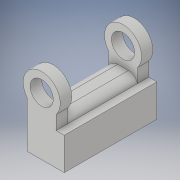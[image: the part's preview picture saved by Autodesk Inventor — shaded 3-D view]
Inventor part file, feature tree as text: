
AUTODESK INVENTOR PART (.ipt)
format: ipt  version: 2019 (Build 230136000, 136)  size: 167,936 bytes
history: native  units: in
note: dims shown in document units (in); Inventor stores cm internally (conversion verified against a paired STEP export)
features: sketch x7, extrude x5, fillet x2
ambient origin geometry x8: Origin, YZ Plane, XZ Plane, XY Plane, X Axis, Y Axis, Z Axis, Center Point
bodies: Solid1 (feature_tree)
feature tree (14):
  extrude  "Extrusion1"  Depth=0.315in
  sketch  "3D Sketch1"
  sketch  "Sketch2"  dims[d5=0.3937in d6=0.7874in d7=0.0in]
  extrude  "Extrusion2"  Depth=0.7874in TaperAngle=0.0deg
  extrude  "Extrusion3"  Depth=0.7874in TaperAngle=0.0deg
  extrude  "Extrusion4"  Depth=0.5935in
  fillet  "Fillet1"  Radius=0.3937in
  fillet  "Fillet2"  Radius=0.2756in
  extrude  "Extrusion5"  Depth=0.315in
  sketch  "Sketch1"  dims[d2=0.315in d3=0.1969in]
  sketch  "Sketch3"  dims[d8=0.7874in d9=0.0in d10=0.0039in d11=0.0in]
  sketch  "Sketch4"  dims[d12=0.315in d13=0.5935in d14=0.3937in d15=0.0in d17=0.2756in]
  sketch  "Sketch5"  dims[d18=0.1181in d19=0.315in]
  sketch  "Sketch6"  dims[d23=0.0787in d24=0.0787in d27=0.3937in d28=0.0in]
